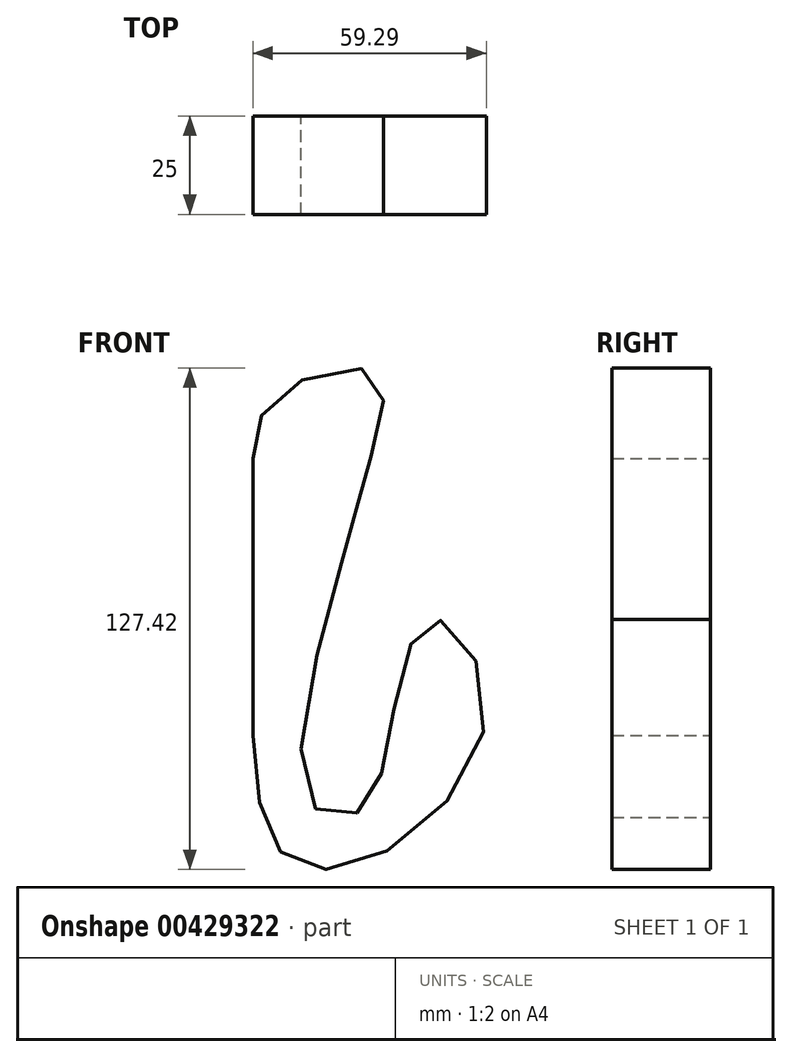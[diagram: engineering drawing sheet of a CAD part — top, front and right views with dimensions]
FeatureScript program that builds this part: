
annotation { "Feature Type Name" : "Feature", "Feature Type Description" : "" }
export const myFeature = defineFeature(function(context is Context, id is Id, definition is map)
    precondition{}
    {
        {
            var Q0;
            Q0=qCreatedBy(makeId("Front.planeOp"),FACE);
            var sketch = newSketch(context, id + "F0", { "sketchPlane" : qUnion([Q0])});
            skLineSegment(sketch, "E0", {"start": v(0, 0) * mm, "end": v(0, -70.38) * mm});
            skFitSpline(sketch, "E1", {"points": [v(0, -70.38) * mm, v(7.25, -100.23) * mm, v(30.7, -101.51) * mm, v(59.29, -63.98) * mm, v(46.06, -40.95) * mm, v(35.83, -63.55) * mm, v(27.3, -89.57) * mm, v(14.08, -86.59) * mm, v(23.46, -23.46) * mm, v(29.86, 0) * mm, v(31.14, 21.33) * mm, v(5.97, 15.78) * mm, v(0, 0) * mm], "startDerivative": vector(25.3, -409) * mm, "endDerivative": vector(-16.55, -258.8) * mm});
            skSolve(sketch);
        }
        {
            var Q0;
            Q0=makeQuery(id+"F0.imprint","IMPRINT",FACE,{"disambiguationData":[TD([[makeQuery(id+"F0.imprint","IMPRINT",EDGE,{"derivedFrom":sQuery(id+"F0.wireOp",EDGE,"E0")}),1.0]])]});
            extrude(context, id + "F1", {"entities" : qUnion([Q0]), "depth" : 25 * mm});
        }
    });
